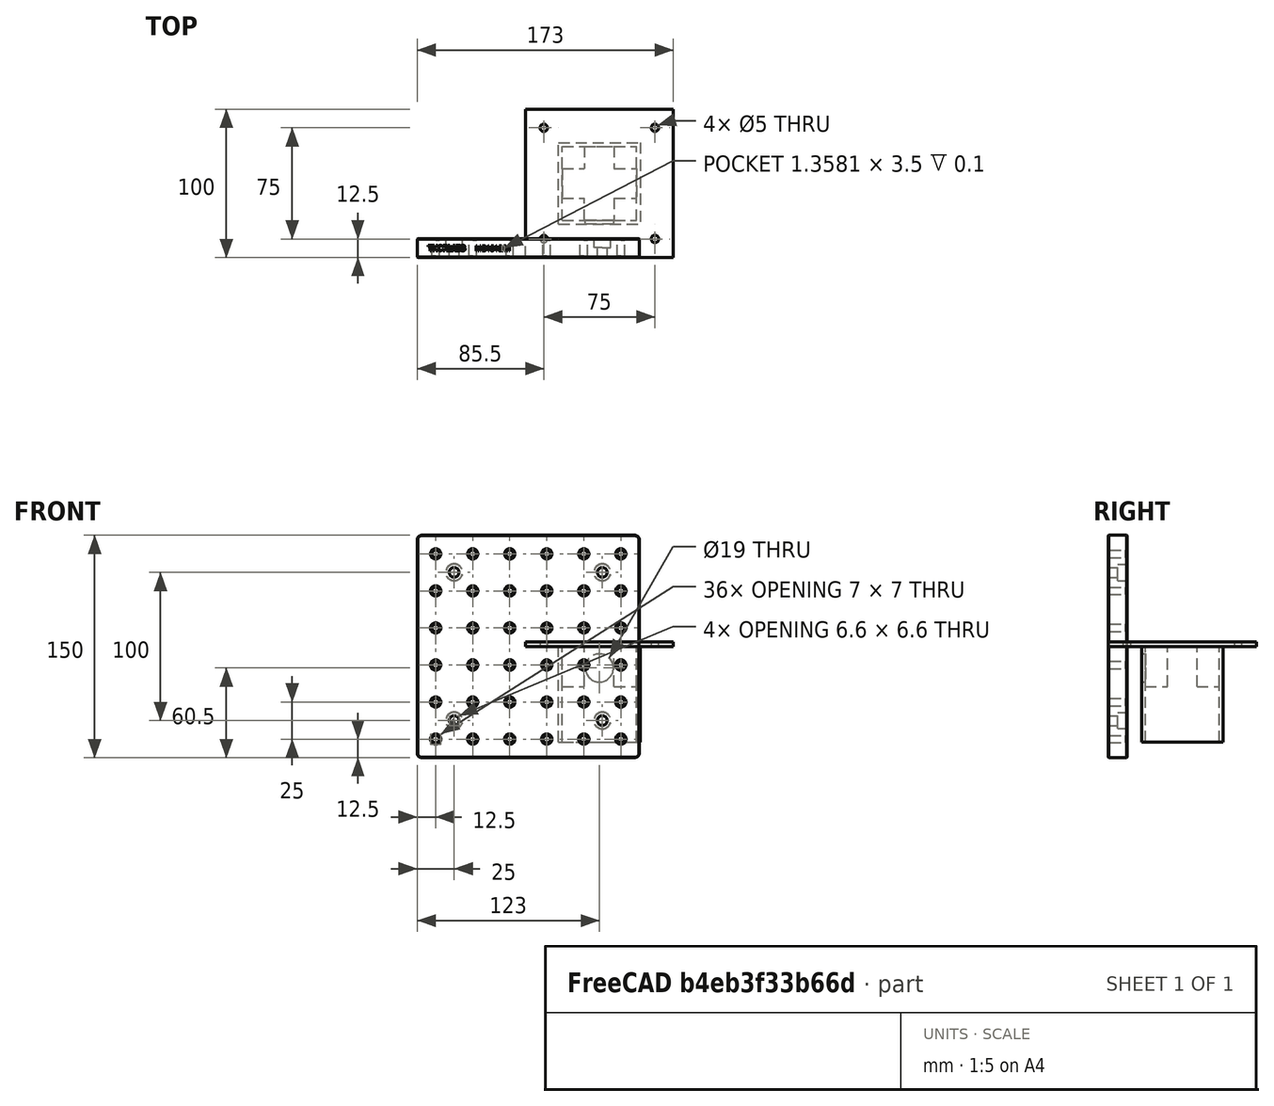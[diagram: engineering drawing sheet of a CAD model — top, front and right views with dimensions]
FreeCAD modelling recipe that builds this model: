
FCSTD DOCUMENT  (FreeCAD 0.21R33694 (Git))
Label: camera_box_v2
License: All rights reserved
LicenseURL: https://en.wikipedia.org/wiki/All_rights_reserved
objects: Part::Box×7, Part::Cylinder×5, Part::MultiFuse×3, Part::Cut×3, Part::Feature×1, App::Part×1
note: 19 computed .brp shape members not serialized (recipe doc carries the construction recipe); baked Part::Feature solids carry a one-line shape summary decoded from their .brp

FEATURE [Part::Box] Box  label="Cube"
  AttacherType = Attacher::AttachEngine3D
  Height = 3
  Length = 100
  Width = 100
FEATURE [Part::Box] Box001  label="Cube001"
  AttacherType = Attacher::AttachEngine3D
  Height = 65
  Length = 55
  Placement = pos=(22.5,22.5,-57) rot=(0,0,1;0rad)
  Width = 55
FEATURE [Part::Box] Box002  label="Cube002"
  AttacherType = Attacher::AttachEngine3D
  Height = 65
  Length = 50
  Placement = pos=(25,25,-57) rot=(0,0,1;0rad)
  Width = 50
FEATURE [Part::Box] Box003  label="Cube003"
  AttacherType = Attacher::AttachEngine3D
  Height = 29
  Length = 15
  Placement = pos=(25,25,-27) rot=(0,0,1;0rad)
  Width = 15
FEATURE [Part::Box] Box004  label="Cube004"
  AttacherType = Attacher::AttachEngine3D
  Height = 29
  Length = 15
  Placement = pos=(25,60,-27) rot=(0,0,1;0rad)
  Width = 15
FEATURE [Part::Box] Box005  label="Cube005"
  AttacherType = Attacher::AttachEngine3D
  Height = 29
  Length = 15
  Placement = pos=(60,60,-27) rot=(0,0,1;0rad)
  Width = 15
FEATURE [Part::Box] Box006  label="Cube006"
  AttacherType = Attacher::AttachEngine3D
  Height = 29
  Length = 15
  Placement = pos=(60,25,-27) rot=(0,0,1;0rad)
  Width = 15
FEATURE [Part::Cylinder] Cylinder
  Angle = 360
  AttacherType = Attacher::AttachEngine3D
  FirstAngle = 0
  Height = 4
  Placement = pos=(50,25.5,-7) rot=(1,0,0;1.5708rad)
  Radius = 9.5
  SecondAngle = 0
FEATURE [Part::Cylinder] Cylinder001
  Angle = 360
  AttacherType = Attacher::AttachEngine3D
  FirstAngle = 0
  Height = 10
  Placement = pos=(12.5,12.5,-3) rot=(0,0,1;0rad)
  Radius = 2.5
  SecondAngle = 0
FEATURE [Part::Cylinder] Cylinder002
  Angle = 360
  AttacherType = Attacher::AttachEngine3D
  FirstAngle = 0
  Height = 10
  Placement = pos=(87.5,12.5,-3) rot=(0,0,1;0rad)
  Radius = 2.5
  SecondAngle = 0
FEATURE [Part::Feature] Part__Feature  label="MB1515_M - Aluminium Breadboard 150 x 150 x 12.7mm_MB3030_M-1"
  Placement = pos=(2,0,0) rot=(0,0,1;0rad)
  shape: bbox 150 x 12.7 x 150 mm, 538 faces (baked)
FEATURE [App::Part] MB1515_M
  Group = -> [Part__Feature]
  Origin = -> Origin
  Placement = pos=(48,50,50) rot=(1,0,0;1.5708rad)
FEATURE [Part::Cylinder] Cylinder003
  Angle = 360
  AttacherType = Attacher::AttachEngine3D
  FirstAngle = 0
  Height = 10
  Placement = pos=(87.5,87.5,-3) rot=(0,0,1;0rad)
  Radius = 2.5
  SecondAngle = 0
FEATURE [Part::Cylinder] Cylinder004
  Angle = 360
  AttacherType = Attacher::AttachEngine3D
  FirstAngle = 0
  Height = 10
  Placement = pos=(12.5,87.5,-3) rot=(0,0,1;0rad)
  Radius = 2.5
  SecondAngle = 0
FEATURE [Part::MultiFuse] Fusion
  Shapes = -> [Cylinder001,Cylinder002,Cylinder003,Cylinder004]
FEATURE [Part::Cut] Cut002
  Base = -> Box
  Tool = -> Fusion
FEATURE [Part::Cut] Cut
  Base = -> Box001
  Tool = -> Box002
FEATURE [Part::Cut] Cut001
  Base = -> Cut
  Placement = pos=(0,0,-7.5) rot=(0,0,1;0rad)
  Tool = -> Cylinder
FEATURE [Part::MultiFuse] Fusion001
  Shapes = -> [Box003,Box004,Box005,Box006,Cut002]
FEATURE [Part::MultiFuse] Fusion002
  Shapes = -> [Cut001,Fusion001]
